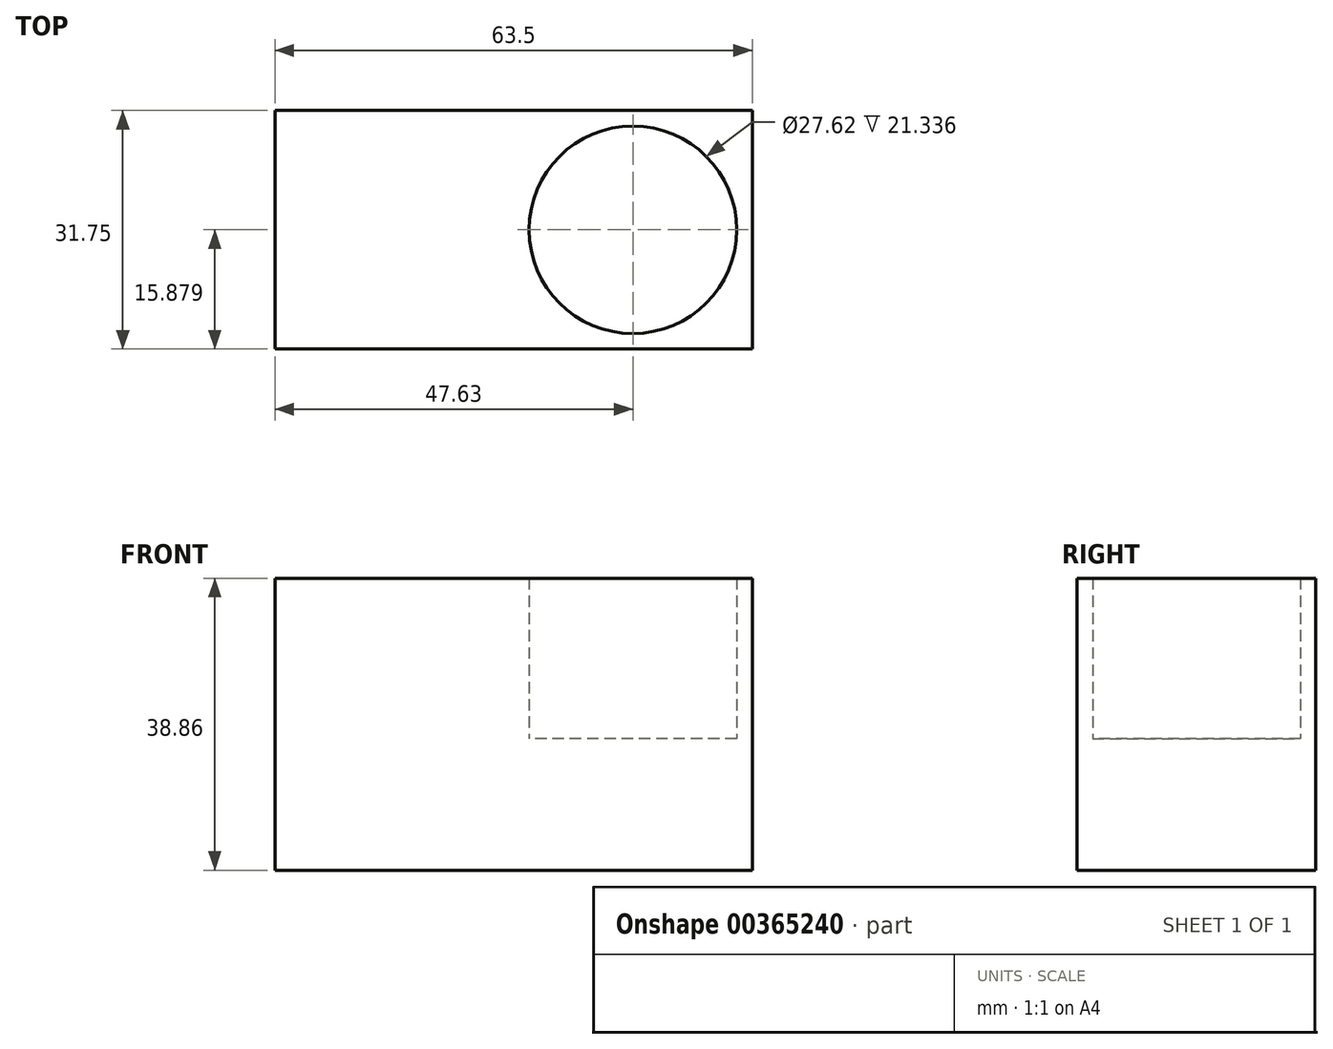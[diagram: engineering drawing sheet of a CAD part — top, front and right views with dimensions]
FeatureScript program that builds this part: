
annotation { "Feature Type Name" : "Feature", "Feature Type Description" : "" }
export const myFeature = defineFeature(function(context is Context, id is Id, definition is map)
    precondition{}
    {
        {
            var Q0;
            Q0=qCreatedBy(makeId("Top.planeOp"),FACE);
            var sketch = newSketch(context, id + "F0", { "sketchPlane" : qUnion([Q0])});
            skLineSegment(sketch, "E0.bottom", {"start": v(-58.37, 43.8) * mm, "end": v(5.13, 43.8) * mm});
            skLineSegment(sketch, "E0.top", {"start": v(-58.37, 12.04) * mm, "end": v(5.13, 12.04) * mm});
            skLineSegment(sketch, "E0.left", {"start": v(-58.37, 43.8) * mm, "end": v(-58.37, 12.04) * mm});
            skLineSegment(sketch, "E0.right", {"start": v(5.13, 43.8) * mm, "end": v(5.13, 12.04) * mm});
            skLineSegment(sketch, "E1.top", {"start": v(-57.1, 19.8) * mm, "end": v(-58.37, 19.8) * mm});
            skLineSegment(sketch, "E1.left", {"start": v(-57.1, 19.92) * mm, "end": v(-57.1, 19.8) * mm});
            skLineSegment(sketch, "E1.right", {"start": v(-58.37, 19.92) * mm, "end": v(-58.37, 19.8) * mm});
            skLineSegment(sketch, "E2.top", {"start": v(-57.1, 36.3) * mm, "end": v(-58.37, 36.3) * mm});
            skLineSegment(sketch, "E2.left", {"start": v(-57.1, 36.17) * mm, "end": v(-57.1, 36.3) * mm});
            skLineSegment(sketch, "E2.right", {"start": v(-58.37, 36.17) * mm, "end": v(-58.37, 36.3) * mm});
            skLineSegment(sketch, "E3.MirrorCS", {"start": v(-57.1, 20.04) * mm, "end": v(-58.37, 20.04) * mm});
            skLineSegment(sketch, "E4.MirrorCS", {"start": v(-57.1, 19.92) * mm, "end": v(-57.1, 20.04) * mm});
            skLineSegment(sketch, "E5.MirrorCS", {"start": v(-57.1, 36.05) * mm, "end": v(-58.37, 36.05) * mm});
            skLineSegment(sketch, "E6.MirrorCS", {"start": v(-57.1, 36.17) * mm, "end": v(-57.1, 36.05) * mm});
            skLineSegment(sketch, "E7", {"start": v(-26.62, 43.8) * mm, "end": v(-26.62, 12.04) * mm});
            skLineSegment(sketch, "E8.MirrorCS", {"start": v(-27.89, 36.3) * mm, "end": v(-26.62, 36.3) * mm});
            skLineSegment(sketch, "E9.MirrorCS", {"start": v(-27.89, 36.05) * mm, "end": v(-26.62, 36.05) * mm});
            skLineSegment(sketch, "E10.MirrorCS", {"start": v(-27.89, 36.17) * mm, "end": v(-27.89, 36.3) * mm});
            skLineSegment(sketch, "E11.MirrorCS", {"start": v(-27.89, 36.17) * mm, "end": v(-27.89, 36.05) * mm});
            skLineSegment(sketch, "E12.MirrorCS", {"start": v(-27.89, 20.04) * mm, "end": v(-26.62, 20.04) * mm});
            skLineSegment(sketch, "E13.MirrorCS", {"start": v(-27.89, 19.8) * mm, "end": v(-26.62, 19.8) * mm});
            skLineSegment(sketch, "E14.MirrorCS", {"start": v(-27.89, 19.92) * mm, "end": v(-27.89, 19.8) * mm});
            skLineSegment(sketch, "E15.MirrorCS", {"start": v(-27.89, 19.92) * mm, "end": v(-27.89, 20.04) * mm});
            skLineSegment(sketch, "E16.bottom", {"start": v(-50.5, 18.4) * mm, "end": v(-50.62, 18.4) * mm});
            skLineSegment(sketch, "E16.top", {"start": v(-50.5, 12.04) * mm, "end": v(-50.62, 12.04) * mm});
            skLineSegment(sketch, "E16.right", {"start": v(-50.62, 18.4) * mm, "end": v(-50.62, 12.04) * mm});
            skLineSegment(sketch, "E17.bottom", {"start": v(-33.22, 18.4) * mm, "end": v(-33.1, 18.4) * mm});
            skLineSegment(sketch, "E17.top", {"start": v(-33.22, 12.04) * mm, "end": v(-33.1, 12.04) * mm});
            skLineSegment(sketch, "E17.right", {"start": v(-33.1, 18.4) * mm, "end": v(-33.1, 12.04) * mm});
            skLineSegment(sketch, "E18.MirrorCS", {"start": v(-50.5, 18.4) * mm, "end": v(-50.36, 18.4) * mm});
            skLineSegment(sketch, "E19.MirrorCS", {"start": v(-50.36, 18.4) * mm, "end": v(-50.36, 12.04) * mm});
            skLineSegment(sketch, "E20.MirrorCS", {"start": v(-33.35, 18.4) * mm, "end": v(-33.35, 12.04) * mm});
            skLineSegment(sketch, "E21.MirrorCS", {"start": v(-33.22, 18.4) * mm, "end": v(-33.35, 18.4) * mm});
            skLineSegment(sketch, "E22.MirrorCS", {"start": v(-33.35, 37.44) * mm, "end": v(-33.35, 43.8) * mm});
            skLineSegment(sketch, "E23.MirrorCS", {"start": v(-33.1, 37.44) * mm, "end": v(-33.1, 43.8) * mm});
            skLineSegment(sketch, "E24.MirrorCS", {"start": v(-33.22, 37.44) * mm, "end": v(-33.35, 37.44) * mm});
            skLineSegment(sketch, "E25.MirrorCS", {"start": v(-33.22, 37.44) * mm, "end": v(-33.1, 37.44) * mm});
            skLineSegment(sketch, "E26.MirrorCS", {"start": v(-50.36, 37.44) * mm, "end": v(-50.36, 43.8) * mm});
            skLineSegment(sketch, "E27.MirrorCS", {"start": v(-50.5, 37.44) * mm, "end": v(-50.36, 37.44) * mm});
            skLineSegment(sketch, "E28.MirrorCS", {"start": v(-50.5, 37.44) * mm, "end": v(-50.62, 37.44) * mm});
            skLineSegment(sketch, "E29.MirrorCS", {"start": v(-50.62, 37.44) * mm, "end": v(-50.62, 43.8) * mm});
            skLineSegment(sketch, "E30.MirrorCS", {"start": v(-25.35, 36.3) * mm, "end": v(-26.62, 36.3) * mm});
            skLineSegment(sketch, "E31.MirrorCS", {"start": v(-25.35, 36.17) * mm, "end": v(-25.35, 36.3) * mm});
            skLineSegment(sketch, "E32.MirrorCS", {"start": v(-25.35, 36.05) * mm, "end": v(-26.62, 36.05) * mm});
            skLineSegment(sketch, "E33.MirrorCS", {"start": v(-25.35, 20.04) * mm, "end": v(-26.62, 20.04) * mm});
            skLineSegment(sketch, "E34.MirrorCS", {"start": v(-25.35, 19.8) * mm, "end": v(-26.62, 19.8) * mm});
            skLineSegment(sketch, "E35.MirrorCS", {"start": v(-25.35, 19.92) * mm, "end": v(-25.35, 19.8) * mm});
            skLineSegment(sketch, "E36.MirrorCS", {"start": v(-25.35, 19.92) * mm, "end": v(-25.35, 20.04) * mm});
            skLineSegment(sketch, "E37.MirrorCS", {"start": v(-20.14, 18.4) * mm, "end": v(-20.14, 12.04) * mm});
            skLineSegment(sketch, "E38.MirrorCS", {"start": v(-19.88, 18.4) * mm, "end": v(-19.88, 12.04) * mm});
            skLineSegment(sketch, "E39.MirrorCS", {"start": v(-20.01, 18.4) * mm, "end": v(-19.88, 18.4) * mm});
            skLineSegment(sketch, "E40.MirrorCS", {"start": v(-20.01, 18.4) * mm, "end": v(-20.14, 18.4) * mm});
            skLineSegment(sketch, "E41.MirrorCS", {"start": v(-2.87, 18.4) * mm, "end": v(-2.87, 12.04) * mm});
            skLineSegment(sketch, "E42.MirrorCS", {"start": v(-2.61, 18.4) * mm, "end": v(-2.61, 12.04) * mm});
            skLineSegment(sketch, "E43.MirrorCS", {"start": v(-2.74, 18.4) * mm, "end": v(-2.61, 18.4) * mm});
            skLineSegment(sketch, "E44.MirrorCS", {"start": v(-2.74, 18.4) * mm, "end": v(-2.87, 18.4) * mm});
            skLineSegment(sketch, "E45.MirrorCS", {"start": v(3.86, 19.8) * mm, "end": v(5.13, 19.8) * mm});
            skLineSegment(sketch, "E46.MirrorCS", {"start": v(3.86, 20.04) * mm, "end": v(5.13, 20.04) * mm});
            skLineSegment(sketch, "E47.MirrorCS", {"start": v(3.86, 19.92) * mm, "end": v(3.86, 20.04) * mm});
            skLineSegment(sketch, "E48.MirrorCS", {"start": v(3.86, 19.92) * mm, "end": v(3.86, 19.8) * mm});
            skLineSegment(sketch, "E49.MirrorCS", {"start": v(3.86, 36.05) * mm, "end": v(5.13, 36.05) * mm});
            skLineSegment(sketch, "E50.MirrorCS", {"start": v(3.86, 36.17) * mm, "end": v(3.86, 36.05) * mm});
            skLineSegment(sketch, "E51.MirrorCS", {"start": v(3.86, 36.17) * mm, "end": v(3.86, 36.3) * mm});
            skLineSegment(sketch, "E52.MirrorCS", {"start": v(3.86, 36.3) * mm, "end": v(5.13, 36.3) * mm});
            skLineSegment(sketch, "E53.MirrorCS", {"start": v(-2.61, 37.44) * mm, "end": v(-2.61, 43.8) * mm});
            skLineSegment(sketch, "E54.MirrorCS", {"start": v(-2.87, 37.44) * mm, "end": v(-2.87, 43.8) * mm});
            skLineSegment(sketch, "E55.MirrorCS", {"start": v(-2.74, 37.44) * mm, "end": v(-2.61, 37.44) * mm});
            skLineSegment(sketch, "E56.MirrorCS", {"start": v(-2.74, 37.44) * mm, "end": v(-2.87, 37.44) * mm});
            skLineSegment(sketch, "E57.MirrorCS", {"start": v(-20.14, 37.44) * mm, "end": v(-20.14, 43.8) * mm});
            skLineSegment(sketch, "E58.MirrorCS", {"start": v(-19.88, 37.44) * mm, "end": v(-19.88, 43.8) * mm});
            skLineSegment(sketch, "E59.MirrorCS", {"start": v(-20.01, 37.44) * mm, "end": v(-19.88, 37.44) * mm});
            skLineSegment(sketch, "E60.MirrorCS", {"start": v(-20.01, 37.44) * mm, "end": v(-20.14, 37.44) * mm});
            skLineSegment(sketch, "E61.MirrorCS", {"start": v(-25.35, 36.17) * mm, "end": v(-25.35, 36.05) * mm});
            skSolve(sketch);
        }
        {
            var Q0;
            Q0 = qSketchRegion(id + "F0", true);
            var Q1;
            {var subQ0=sQuery(id+"F0.wireOp",EDGE,"E8.MirrorCS");Q1=makeQuery(id+"F0.imprint","IMPRINT",FACE,{"disambiguationData":[TD([[makeQuery(id+"F0.imprint","IMPRINT",EDGE,{"derivedFrom":subQ0}),-1.0]])]});}
            var Q2;
            {var subQ1=sQuery(id+"F0.wireOp",EDGE,"E30.MirrorCS");Q2=makeQuery(id+"F0.imprint","IMPRINT",FACE,{"disambiguationData":[TD([[makeQuery(id+"F0.imprint","IMPRINT",EDGE,{"derivedFrom":subQ1}),1.0]])]});}
            var Q3;
            {var subQ0=sQuery(id+"F0.wireOp",EDGE,"E33.MirrorCS");Q3=makeQuery(id+"F0.imprint","IMPRINT",FACE,{"disambiguationData":[TD([[makeQuery(id+"F0.imprint","IMPRINT",EDGE,{"derivedFrom":subQ0}),1.0]])]});}
            var Q4;
            {var subQ1=sQuery(id+"F0.wireOp",EDGE,"E12.MirrorCS");Q4=makeQuery(id+"F0.imprint","IMPRINT",FACE,{"disambiguationData":[TD([[makeQuery(id+"F0.imprint","IMPRINT",EDGE,{"derivedFrom":subQ1}),-1.0]])]});}
            extrude(context, id + "F1", {"entities" : qUnion([Q0, Q1, Q2, Q3, Q4]), "depth" : 17.53 * mm});
        }
        {
            var Q0;
            Q0=makeQuery(id+"F1.opExtrude","CAP_FACE",FACE,{"disambiguationData":[OSD([sQuery(id+"F0.wireOp",EDGE,"E0.bottom"),sQuery(id+"F0.wireOp",EDGE,"E0.top"),sQuery(id+"F0.wireOp",EDGE,"E0.left"),sQuery(id+"F0.wireOp",EDGE,"E0.right"),sQuery(id+"F0.wireOp",EDGE,"E1.right"),sQuery(id+"F0.wireOp",EDGE,"E2.right"),sQuery(id+"F0.wireOp",EDGE,"E16.top"),sQuery(id+"F0.wireOp",EDGE,"E17.top")])],"isStart":false});
            var sketch = newSketch(context, id + "F2", { "sketchPlane" : qUnion([Q0])});
            skCircle(sketch, "E62", {"center": v(-42.5, 27.92) * mm, "radius": 13.8 * mm});
            skCircle(sketch, "E63.MirrorC", {"center": v(-10.74, 27.92) * mm, "radius": 13.8 * mm});
            skSolve(sketch);
        }
        {
            var Q0;
            Q0=makeQuery(id+"F2.imprint","IMPRINT",FACE,{"disambiguationData":[TD([[makeQuery(id+"F2.imprint","IMPRINT",EDGE,{"derivedFrom":sQuery(id+"F2.wireOp",EDGE,"E62")}),1.0]])]});
            var Q1;
            Q1=makeQuery(id+"F2.imprint","IMPRINT",FACE,{"disambiguationData":[TD([[makeQuery(id+"F2.imprint","IMPRINT",EDGE,{"derivedFrom":sQuery(id+"F2.wireOp",EDGE,"E63.MirrorC")}),-1.0]])]});
            extrude(context, id + "F3", {"entities" : qUnion([Q0, Q1]), "operationType" : NewBodyOperationType.ADD, "depth" : 21.34 * mm});
        }
    });
